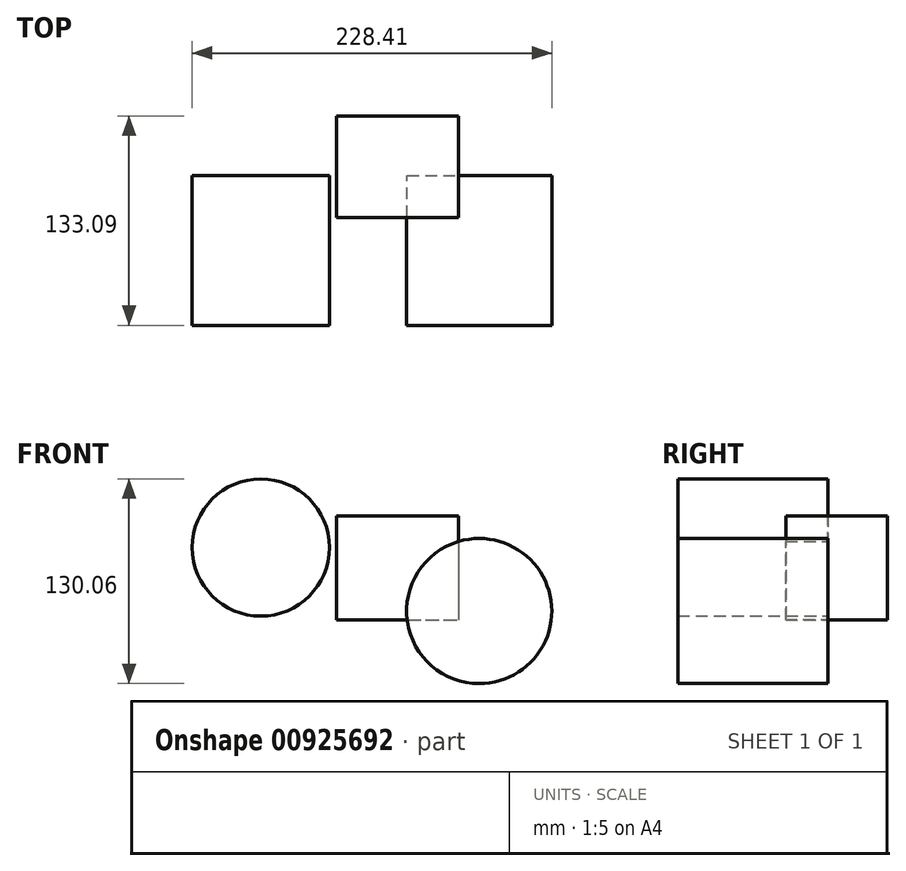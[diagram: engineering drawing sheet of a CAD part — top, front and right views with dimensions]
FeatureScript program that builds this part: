
annotation { "Feature Type Name" : "Feature", "Feature Type Description" : "" }
export const myFeature = defineFeature(function(context is Context, id is Id, definition is map)
    precondition{}
    {
        {
            var Q0;
            Q0=qCreatedBy(makeId("Top.planeOp"),FACE);
            var sketch = newSketch(context, id + "F0", { "sketchPlane" : qUnion([Q0])});
            skLineSegment(sketch, "E0.bottom", {"start": v(-115.32, 37.84) * mm, "end": v(-37.85, 37.84) * mm});
            skLineSegment(sketch, "E0.top", {"start": v(-115.32, -26.59) * mm, "end": v(-37.85, -26.59) * mm});
            skLineSegment(sketch, "E0.left", {"start": v(-115.32, 37.84) * mm, "end": v(-115.32, -26.59) * mm});
            skLineSegment(sketch, "E0.right", {"start": v(-37.85, 37.84) * mm, "end": v(-37.85, -26.59) * mm});
            skSolve(sketch);
        }
        {
            var Q0;
            Q0 = qSketchRegion(id + "F0", true);
            extrude(context, id + "F1", {"entities" : qUnion([Q0]), "depth" : 66.3 * mm, "offsetDistance" : 25.4 * mm});
        }
        {
            var Q0;
            Q0=qCreatedBy(makeId("Front.planeOp"),FACE);
            var sketch = newSketch(context, id + "F2", { "sketchPlane" : qUnion([Q0])});
            skCircle(sketch, "E1", {"center": v(-163.45, 46.14) * mm, "radius": 43.6 * mm});
            skCircle(sketch, "E2", {"center": v(-24.72, 5.77) * mm, "radius": 46.1 * mm});
            skSolve(sketch);
        }
        {
            var Q0;
            Q0=makeQuery(id+"F2.imprint","IMPRINT",FACE,{"disambiguationData":[TD([[makeQuery(id+"F2.imprint","IMPRINT",EDGE,{"derivedFrom":sQuery(id+"F2.wireOp",EDGE,"E2")}),1.0]])]});
            var Q1;
            Q1=makeQuery(id+"F2.imprint","IMPRINT",FACE,{"disambiguationData":[TD([[makeQuery(id+"F2.imprint","IMPRINT",EDGE,{"derivedFrom":sQuery(id+"F2.wireOp",EDGE,"E1")}),1.0]])]});
            extrude(context, id + "F3", {"entities" : qUnion([Q0, Q1]), "operationType" : NewBodyOperationType.ADD, "depth" : 95.25 * mm, "offsetDistance" : 25.4 * mm});
        }
    });
